# Revit family: QF_ZANUSSI_102081_CRF2420B20N
name_source: partatom
category: Attrezzature speciali
units: mm (PartAtom-declared; Revit-internal decimal feet)

## family parameters
Basato su piano di lavoro = No
Condiviso = No
Punto di calcolo locali = No
Quota connettore circolare = Usa diametro
Sempre verticale = Sì
Taglio con vuoti quando caricato = No
Tipo di parte = Normale

## types (1)
- Standard
    Accessory = Sì
    Cold Water Size = 0 mm
    Compressed Air Pressure = 0.0 Pa
    Compressed Air Size = 0 mm
    Compressed Air Volume = 0.0 L/s
    Condensate Return Size = 0 mm
    Cycle = 50 Hz
    Depth = 2630 mm  [stored 8.62861 ft]
    Depth Actual = 2630 mm  [stored 8.62861 ft]
    Descrizione = COLDROOM 203x243 -18-20°C BUILT-IN UNIT
    Direct Waste Size = 0 mm
    Gas Input Pressure = 0
    Gas KW = 0
    Gas Size = 0 mm
    HP = 2.6 HP
    Height = 2230 mm  [stored 7.31627 ft]
    Height Actual = 2230 mm  [stored 7.31627 ft]
    Hot Water Size = 0 mm
    Item Number = 102081
    Length Actual = 2230 mm  [stored 7.31627 ft]
    Modello = CRF2420B20N
    Phase = 1
    Produttore = Zanussi
    Prospetto di default = 0 mm  [stored 0 ft]
    Refrigerant Compressor Remote = Sì
    Refrigeration Liquid Line Size = 0 mm  [stored 0 ft]
    Refrigeration Suction Line Size = 0 mm  [stored 0 ft]
    Steam Consumption per Hour = 0
    Steam Supply Maximum Pressure = 0.0 Pa
    Steam Supply Minimum Pressure = 0.0 Pa
    Steam Supply Size = 0 mm
    URL = http://www.zanussiprofessional.com
    URL Manufacturer = http://www.zanussiprofessional.com
    Volts = 220 V
    Watts = 1960 W
    Weight = 481.10 kg
    Width = 2230 mm  [stored 7.31627 ft]

note: source unit labels omitted for Gas Input Pressure — the stored unit's dimension contradicts the parameter name (converter mislabeling)

note: [stored X ft] marks values corroborated as IEEE doubles in the binary element streams (Revit-internal decimal feet)

## geometry (parser evidence)
native form markers: Sweep x7
no freeform markers — native parametric forms only
